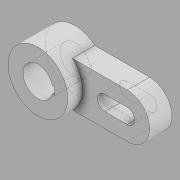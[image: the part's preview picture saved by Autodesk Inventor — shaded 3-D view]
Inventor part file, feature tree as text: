
AUTODESK INVENTOR PART (.ipt)
format: ipt  version: 2020 (Build 240168000, 168)  size: 136,192 bytes
history: native  units: mm
features: extrude x2, sketch x2, other x1
ambient origin geometry x8: Origin, YZ Plane, XZ Plane, XY Plane, X Axis, Y Axis, Z Axis, Center Point
bodies: Body1 (feature_tree)
feature tree (5):
  other  "Sólido1"
  extrude  "Extrusión1"  Depth=40.0mm
  extrude  "Extrusión2"  Depth=20.0mm
  sketch  "Boceto1"  dims[d0=80.0mm d1=40.0mm]
  sketch  "Boceto2"  dims[d3=10.0mm d4=130.0mm d5=60.0mm d7=30.0mm d8=50.0mm d9=20.0mm d10=85.0mm d11=10.0mm d12=10.0mm d13=30.0mm d14=0.0mm d16=10.0mm d18=0.0mm d19=20.0mm d20=0.0mm d15=0.5mm]
